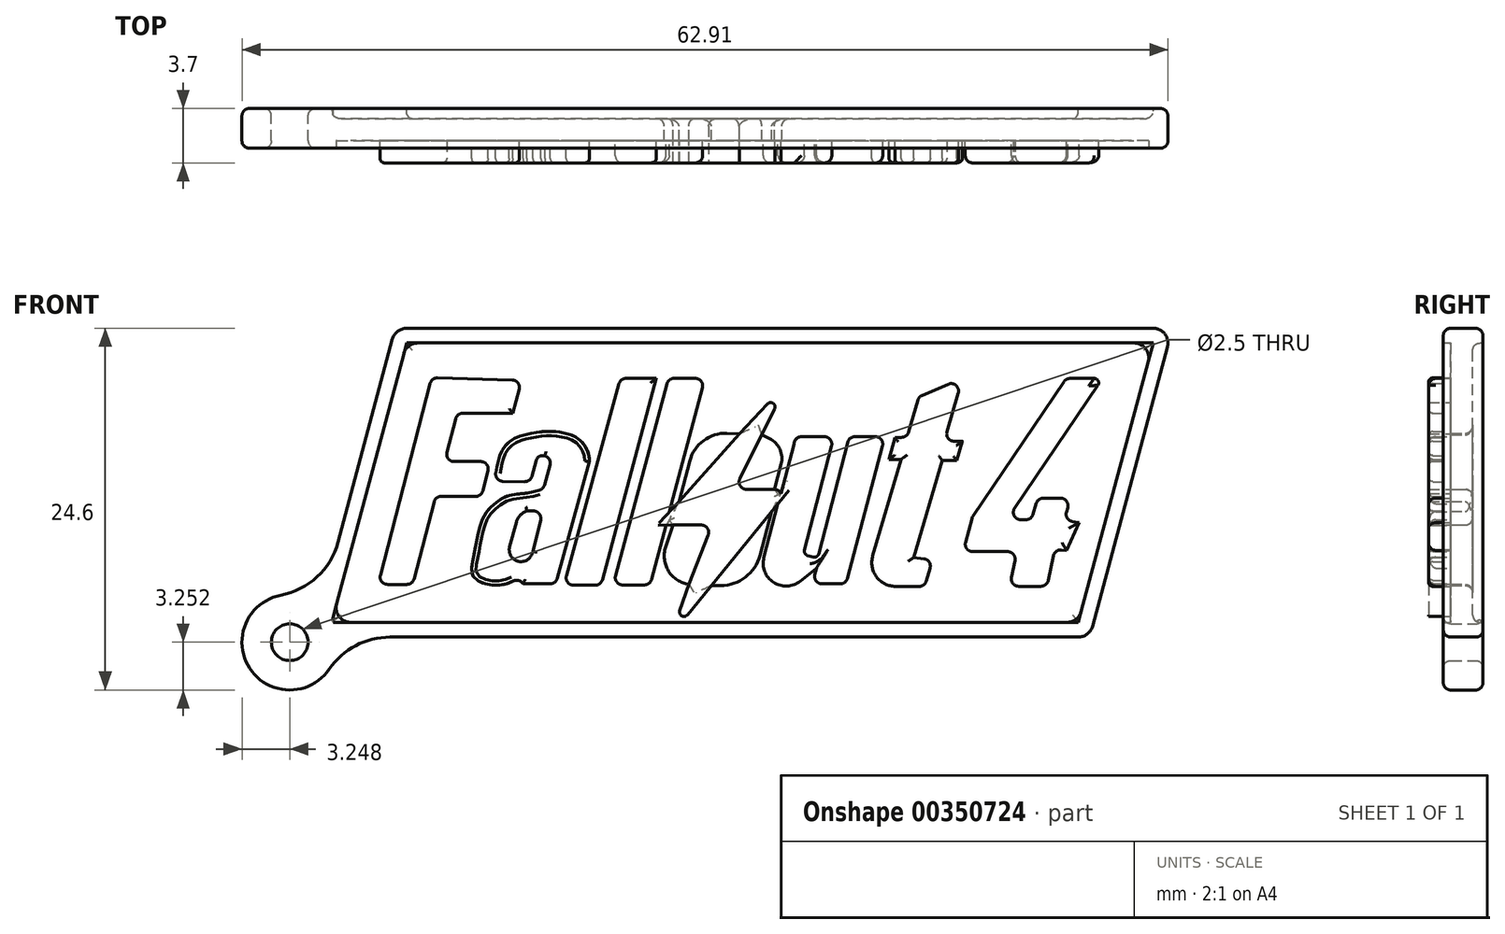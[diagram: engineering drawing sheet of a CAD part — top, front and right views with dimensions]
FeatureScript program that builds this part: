
annotation { "Feature Type Name" : "Feature", "Feature Type Description" : "" }
export const myFeature = defineFeature(function(context is Context, id is Id, definition is map)
    precondition{}
    {
        {
            var Q0;
            Q0=qCreatedBy(makeId("Front.planeOp"),FACE);
            var sketch = newSketch(context, id + "F0", { "sketchPlane" : qUnion([Q0])});
            skLineSegment(sketch, "E0", {"start": v(-23.37, 27.5) * mm, "end": v(29.43, 27.5) * mm});
            skLineSegment(sketch, "E1", {"start": v(29.43, 27.5) * mm, "end": v(23.8, 6.5) * mm});
            skLineSegment(sketch, "E2", {"start": v(23.8, 6.5) * mm, "end": v(-29, 6.5) * mm});
            skLineSegment(sketch, "E3", {"start": v(-29, 6.5) * mm, "end": v(-23.37, 27.5) * mm});
            skLineSegment(sketch, "E4", {"start": v(-20.9, 24.14) * mm, "end": v(-24.55, 10.08) * mm});
            skLineSegment(sketch, "E5", {"start": v(-24.55, 10.08) * mm, "end": v(-22.2, 10.08) * mm});
            skLineSegment(sketch, "E6", {"start": v(-22.2, 10.08) * mm, "end": v(-20.64, 16.07) * mm});
            skLineSegment(sketch, "E7", {"start": v(-20.64, 16.07) * mm, "end": v(-17.53, 16.07) * mm});
            skLineSegment(sketch, "E8", {"start": v(-17.53, 16.07) * mm, "end": v(-16.92, 18.43) * mm});
            skLineSegment(sketch, "E9", {"start": v(-16.92, 18.43) * mm, "end": v(-20.03, 18.43) * mm});
            skLineSegment(sketch, "E10", {"start": v(-20.03, 18.43) * mm, "end": v(-19.17, 21.72) * mm});
            skLineSegment(sketch, "E11", {"start": v(-19.17, 21.72) * mm, "end": v(-15.38, 21.72) * mm});
            skLineSegment(sketch, "E12", {"start": v(-15.38, 21.72) * mm, "end": v(-14.8, 23.97) * mm});
            skLineSegment(sketch, "E13", {"start": v(-14.8, 23.97) * mm, "end": v(-20.9, 24.14) * mm});
            skFitSpline(sketch, "E14", {"points": [v(-16.65, 17.1) * mm, v(-16.18, 19.06) * mm, v(-15.46, 19.9) * mm, v(-14.06, 20.38) * mm, v(-12.35, 20.46) * mm, v(-10.83, 19.9) * mm, v(-10.23, 18.9) * mm, v(-10.2, 18.43) * mm], "startDerivative": vector(2.12, 12.27) * mm, "endDerivative": vector(-0.12, -4.9) * mm});
            skLineSegment(sketch, "E15", {"start": v(-10.2, 18.43) * mm, "end": v(-12.47, 10.12) * mm});
            skLineSegment(sketch, "E16", {"start": v(-12.47, 10.12) * mm, "end": v(-14.7, 10.12) * mm});
            skLineSegment(sketch, "E17", {"start": v(-14.7, 10.12) * mm, "end": v(-14.7, 10.72) * mm});
            skFitSpline(sketch, "E18", {"points": [v(-14.7, 10.72) * mm, v(-15.82, 10.12) * mm, v(-17.3, 10.12) * mm, v(-18.13, 10.72) * mm, v(-18.1, 11.8) * mm, v(-17.37, 14.67) * mm, v(-16.53, 15.63) * mm, v(-15.74, 16.1) * mm, v(-14.38, 16.3) * mm, v(-13.33, 16.53) * mm], "startDerivative": vector(-9.58, -6.56) * mm, "endDerivative": vector(9.96, 0.8) * mm});
            skLineSegment(sketch, "E19", {"start": v(-13.33, 16.53) * mm, "end": v(-12.86, 18.22) * mm});
            skLineSegment(sketch, "E20", {"start": v(-13.2, 18.83) * mm, "end": v(-13.2, 18.83) * mm});
            skLineSegment(sketch, "E21", {"start": v(-13.82, 18.48) * mm, "end": v(-14.2, 17.06) * mm});
            skLineSegment(sketch, "E22", {"start": v(-14.2, 17.06) * mm, "end": v(-16.65, 17.1) * mm});
            skPoint(sketch, "E23.visualSharp", {"position": v(-15.68, 15.01) * mm});
            skLineSegment(sketch, "E24", {"start": v(-8.07, 24.1) * mm, "end": v(-11.92, 10.02) * mm});
            skLineSegment(sketch, "E25", {"start": v(-11.92, 10.02) * mm, "end": v(-9.4, 10.02) * mm});
            skLineSegment(sketch, "E26", {"start": v(-9.4, 10.02) * mm, "end": v(-5.64, 24.1) * mm});
            skLineSegment(sketch, "E27", {"start": v(-5.64, 24.1) * mm, "end": v(-8.07, 24.1) * mm});
            skPoint(sketch, "E28.visualSharp", {"position": v(-13.69, 18.96) * mm});
            skArc(sketch, "E28.filletArc", {"start": v(-13.2, 18.83) * mm, "mid": v(-13.59, 18.78) * mm, "end": v(-13.82, 18.48) * mm});
            skPoint(sketch, "E29.visualSharp", {"position": v(-12.73, 18.7) * mm});
            skArc(sketch, "E29.filletArc", {"start": v(-12.86, 18.22) * mm, "mid": v(-12.91, 18.6) * mm, "end": v(-13.21, 18.83) * mm});
            skArc(sketch, "E30.filletArc", {"start": v(-13.2, 18.83) * mm, "mid": v(-13.2, 18.83) * mm, "end": v(-13.2, 18.83) * mm});
            skLineSegment(sketch, "E31", {"start": v(-4.82, 24.1) * mm, "end": v(-8.58, 10.05) * mm});
            skLineSegment(sketch, "E32", {"start": v(-8.58, 10.05) * mm, "end": v(-6.06, 10.05) * mm});
            skLineSegment(sketch, "E33", {"start": v(-6.06, 10.05) * mm, "end": v(-2.34, 24.1) * mm});
            skLineSegment(sketch, "E34", {"start": v(-2.34, 24.1) * mm, "end": v(-4.82, 24.1) * mm});
            skLineSegment(sketch, "E35", {"start": v(-3.37, 18.47) * mm, "end": v(-4.1, 15.72) * mm});
            skLineSegment(sketch, "E36", {"start": v(-4.1, 15.72) * mm, "end": v(-4.75, 15.03) * mm});
            skLineSegment(sketch, "E37", {"start": v(-4.99, 14.11) * mm, "end": v(-4.5, 14.12) * mm});
            skLineSegment(sketch, "E38", {"start": v(-4.5, 14.12) * mm, "end": v(-5, 12.61) * mm});
            skLineSegment(sketch, "E39", {"start": v(-3.42, 10.08) * mm, "end": v(-4.04, 8.3) * mm});
            skLineSegment(sketch, "E40", {"start": v(-3.53, 8) * mm, "end": v(2.77, 15.73) * mm});
            skLineSegment(sketch, "E41", {"start": v(2.38, 16.55) * mm, "end": v(-0.32, 16.55) * mm});
            skLineSegment(sketch, "E42", {"start": v(-0.32, 16.55) * mm, "end": v(2.4, 22.01) * mm});
            skLineSegment(sketch, "E43", {"start": v(1.92, 22.35) * mm, "end": v(0, 20.34) * mm});
            skLineSegment(sketch, "E44", {"start": v(0, 20.34) * mm, "end": v(-0.84, 20.36) * mm});
            skArc(sketch, "E45", {"start": v(-0.84, 20.36) * mm, "mid": v(-2.43, 19.86) * mm, "end": v(-3.37, 18.47) * mm});
            skArc(sketch, "E46", {"start": v(-5, 12.61) * mm, "mid": v(-4.8, 10.98) * mm, "end": v(-3.42, 10.08) * mm});
            skLineSegment(sketch, "E47", {"start": v(-1.9, 10) * mm, "end": v(-1.26, 10) * mm});
            skLineSegment(sketch, "E48", {"start": v(2.2, 15.04) * mm, "end": v(1.4, 12.05) * mm});
            skArc(sketch, "E49", {"start": v(-1.26, 10) * mm, "mid": v(0.42, 10.58) * mm, "end": v(1.4, 12.05) * mm});
            skLineSegment(sketch, "E50", {"start": v(2.38, 16.55) * mm, "end": v(2.84, 18.25) * mm});
            skLineSegment(sketch, "E51", {"start": v(1.53, 20.26) * mm, "end": v(2.05, 20) * mm});
            skArc(sketch, "E52", {"start": v(2.84, 18.25) * mm, "mid": v(2.76, 19.26) * mm, "end": v(2.05, 20) * mm});
            skPoint(sketch, "E53.visualSharp", {"position": v(3.43, 16.55) * mm});
            skArc(sketch, "E53.filletArc", {"start": v(2.77, 15.73) * mm, "mid": v(2.83, 16.26) * mm, "end": v(2.38, 16.55) * mm});
            skPoint(sketch, "E54.visualSharp", {"position": v(-4.6, 6.7) * mm});
            skArc(sketch, "E54.filletArc", {"start": v(-4.04, 8.3) * mm, "mid": v(-3.9, 7.94) * mm, "end": v(-3.53, 8) * mm});
            skPoint(sketch, "E55.visualSharp", {"position": v(3.3, 23.8) * mm});
            skArc(sketch, "E55.filletArc", {"start": v(2.4, 22.01) * mm, "mid": v(2.3, 22.4) * mm, "end": v(1.92, 22.35) * mm});
            skLineSegment(sketch, "E56", {"start": v(3.84, 20.13) * mm, "end": v(2.83, 16.26) * mm});
            skLineSegment(sketch, "E57", {"start": v(2.63, 15.55) * mm, "end": v(1.67, 11.9) * mm});
            skLineSegment(sketch, "E58", {"start": v(3.84, 20.13) * mm, "end": v(6.43, 20.13) * mm});
            skLineSegment(sketch, "E59", {"start": v(6.43, 20.13) * mm, "end": v(4.43, 12.41) * mm});
            skLineSegment(sketch, "E60", {"start": v(4.64, 12.05) * mm, "end": v(5.03, 11.95) * mm});
            skLineSegment(sketch, "E61", {"start": v(5.4, 12.16) * mm, "end": v(7.46, 20.13) * mm});
            skLineSegment(sketch, "E62", {"start": v(7.46, 20.13) * mm, "end": v(9.9, 20.13) * mm});
            skLineSegment(sketch, "E63", {"start": v(9.9, 20.13) * mm, "end": v(7.25, 10.12) * mm});
            skLineSegment(sketch, "E64", {"start": v(7.25, 10.12) * mm, "end": v(5, 10.12) * mm});
            skLineSegment(sketch, "E65", {"start": v(5, 10.12) * mm, "end": v(5.23, 11.18) * mm});
            skLineSegment(sketch, "E66", {"start": v(5.23, 11.18) * mm, "end": v(4.13, 10.3) * mm});
            skArc(sketch, "E67", {"start": v(1.67, 11.9) * mm, "mid": v(2.33, 10.22) * mm, "end": v(4.13, 10.3) * mm});
            skPoint(sketch, "E68.visualSharp", {"position": v(4.35, 12.12) * mm});
            skArc(sketch, "E68.filletArc", {"start": v(4.43, 12.41) * mm, "mid": v(4.46, 12.18) * mm, "end": v(4.64, 12.05) * mm});
            skPoint(sketch, "E69.visualSharp", {"position": v(5.32, 11.87) * mm});
            skArc(sketch, "E69.filletArc", {"start": v(5.03, 11.95) * mm, "mid": v(5.26, 11.98) * mm, "end": v(5.4, 12.16) * mm});
            skLineSegment(sketch, "E70", {"start": v(15.17, 24.12) * mm, "end": v(12.2, 22.84) * mm});
            skLineSegment(sketch, "E71", {"start": v(12.2, 22.84) * mm, "end": v(11.4, 20.08) * mm});
            skLineSegment(sketch, "E72", {"start": v(11.4, 20.08) * mm, "end": v(10.57, 20.08) * mm});
            skLineSegment(sketch, "E73", {"start": v(10.57, 20.08) * mm, "end": v(10.17, 18.58) * mm});
            skLineSegment(sketch, "E74", {"start": v(10.17, 18.58) * mm, "end": v(11, 18.58) * mm});
            skLineSegment(sketch, "E75", {"start": v(11, 18.58) * mm, "end": v(9.06, 12.03) * mm});
            skLineSegment(sketch, "E76", {"start": v(10.63, 9.94) * mm, "end": v(12.6, 9.94) * mm});
            skLineSegment(sketch, "E77", {"start": v(12.6, 9.94) * mm, "end": v(13.12, 11.76) * mm});
            skLineSegment(sketch, "E78", {"start": v(13.12, 11.76) * mm, "end": v(11.86, 11.91) * mm});
            skLineSegment(sketch, "E79", {"start": v(11.86, 11.91) * mm, "end": v(13.8, 18.5) * mm});
            skLineSegment(sketch, "E80", {"start": v(13.8, 18.5) * mm, "end": v(14.77, 18.5) * mm});
            skLineSegment(sketch, "E81", {"start": v(14.77, 18.5) * mm, "end": v(15.15, 19.82) * mm});
            skLineSegment(sketch, "E82", {"start": v(15.15, 19.82) * mm, "end": v(13.92, 19.82) * mm});
            skLineSegment(sketch, "E83", {"start": v(13.92, 19.82) * mm, "end": v(15.17, 24.12) * mm});
            skArc(sketch, "E84", {"start": v(9.06, 12.03) * mm, "mid": v(9.32, 10.6) * mm, "end": v(10.63, 9.94) * mm});
            skCircle(sketch, "E85", {"center": v(15.6, 22.92) * mm, "radius": 0.4 * mm});
            skLineSegment(sketch, "E86", {"start": v(22.2, 24.09) * mm, "end": v(15.83, 14.66) * mm});
            skLineSegment(sketch, "E87", {"start": v(15.83, 14.66) * mm, "end": v(15.2, 12.3) * mm});
            skLineSegment(sketch, "E88", {"start": v(15.2, 12.3) * mm, "end": v(18.85, 12.3) * mm});
            skLineSegment(sketch, "E89", {"start": v(18.85, 12.3) * mm, "end": v(18.37, 9.95) * mm});
            skLineSegment(sketch, "E90", {"start": v(18.37, 9.95) * mm, "end": v(20.91, 9.95) * mm});
            skLineSegment(sketch, "E91", {"start": v(20.91, 9.95) * mm, "end": v(21.43, 12.46) * mm});
            skLineSegment(sketch, "E92", {"start": v(21.43, 12.46) * mm, "end": v(22.24, 12.4) * mm});
            skLineSegment(sketch, "E93", {"start": v(22.24, 12.4) * mm, "end": v(23.1, 14.29) * mm});
            skLineSegment(sketch, "E94", {"start": v(23.1, 14.29) * mm, "end": v(22.07, 14.45) * mm});
            skLineSegment(sketch, "E95", {"start": v(22.07, 14.45) * mm, "end": v(22.5, 15.95) * mm});
            skLineSegment(sketch, "E96", {"start": v(22.5, 15.95) * mm, "end": v(20.28, 15.95) * mm});
            skLineSegment(sketch, "E97", {"start": v(20.28, 15.95) * mm, "end": v(19.85, 14.48) * mm});
            skLineSegment(sketch, "E98", {"start": v(19.85, 14.48) * mm, "end": v(18.18, 14.48) * mm});
            skLineSegment(sketch, "E99", {"start": v(18.18, 14.48) * mm, "end": v(24.37, 23.62) * mm});
            skLineSegment(sketch, "E100", {"start": v(24.12, 24.09) * mm, "end": v(22.2, 24.09) * mm});
            skPoint(sketch, "E101.visualSharp", {"position": v(24.68, 24.09) * mm});
            skArc(sketch, "E101.filletArc", {"start": v(24.37, 23.62) * mm, "mid": v(24.38, 23.93) * mm, "end": v(24.12, 24.09) * mm});
            skLineSegment(sketch, "E102.0", {"start": v(-22.6, 26.5) * mm, "end": v(28.12, 26.5) * mm});
            skLineSegment(sketch, "E102.1", {"start": v(-27.7, 7.5) * mm, "end": v(-22.6, 26.5) * mm});
            skLineSegment(sketch, "E102.2", {"start": v(23.03, 7.5) * mm, "end": v(-27.7, 7.5) * mm});
            skLineSegment(sketch, "E102.3", {"start": v(28.12, 26.5) * mm, "end": v(23.03, 7.5) * mm});
            skLineSegment(sketch, "E103", {"start": v(-4.1, 15.72) * mm, "end": v(0, 20.34) * mm});
            skLineSegment(sketch, "E104", {"start": v(-4.5, 14.12) * mm, "end": v(-1.85, 14.12) * mm});
            skLineSegment(sketch, "E105", {"start": v(-1.85, 14.12) * mm, "end": v(-3.42, 10.08) * mm});
            skLineSegment(sketch, "E106", {"start": v(-13.34, 15.08) * mm, "end": v(-14.04, 12.33) * mm});
            skLineSegment(sketch, "E107", {"start": v(-13.34, 15.08) * mm, "end": v(-14.44, 15.08) * mm});
            skLineSegment(sketch, "E108", {"start": v(-15.14, 14.32) * mm, "end": v(-15.6, 12.64) * mm});
            skArc(sketch, "E109", {"start": v(-14.44, 15.08) * mm, "mid": v(-14.88, 14.78) * mm, "end": v(-15.14, 14.32) * mm});
            skArc(sketch, "E110", {"start": v(-15.6, 12.64) * mm, "mid": v(-14.99, 11.65) * mm, "end": v(-14.04, 12.33) * mm});
            skSolve(sketch);
        }
        {
            var Q0;
            Q0=makeQuery(id+"F0.imprint","IMPRINT",FACE,{"disambiguationData":[TD([[makeQuery(id+"F0.imprint","IMPRINT",EDGE,{"derivedFrom":sQuery(id+"F0.wireOp",EDGE,"E4")}),1.0]])]});
            var Q1;
            Q1=makeQuery(id+"F0.imprint","IMPRINT",FACE,{"disambiguationData":[TD([[makeQuery(id+"F0.imprint","IMPRINT",EDGE,{"derivedFrom":sQuery(id+"F0.wireOp",EDGE,"E14")}),-1.0]])]});
            var Q2;
            Q2=makeQuery(id+"F0.imprint","IMPRINT",FACE,{"disambiguationData":[TD([[makeQuery(id+"F0.imprint","IMPRINT",EDGE,{"derivedFrom":sQuery(id+"F0.wireOp",EDGE,"E24")}),1.0]])]});
            var Q3;
            Q3=makeQuery(id+"F0.imprint","IMPRINT",FACE,{"disambiguationData":[TD([[makeQuery(id+"F0.imprint","IMPRINT",EDGE,{"derivedFrom":sQuery(id+"F0.wireOp",EDGE,"E31")}),1.0]])]});
            var Q4;
            {var subQ12=sQuery(id+"F0.wireOp",EDGE,"E36");Q4=makeQuery(id+"F0.imprint","IMPRINT",FACE,{"disambiguationData":[TD([[makeQuery(id+"F0.imprint","IMPRINT",EDGE,{"derivedFrom":subQ12}),1.0]])]});}
            var Q5;
            {var subQ4=sQuery(id+"F0.wireOp",EDGE,"E56");Q5=makeQuery(id+"F0.imprint","IMPRINT",FACE,{"disambiguationData":[TD([[makeQuery(id+"F0.imprint","IMPRINT",EDGE,{"derivedFrom":subQ4}),1.0]])]});}
            var Q6;
            Q6=makeQuery(id+"F0.imprint","IMPRINT",FACE,{"disambiguationData":[TD([[makeQuery(id+"F0.imprint","IMPRINT",EDGE,{"derivedFrom":sQuery(id+"F0.wireOp",EDGE,"E70")}),1.0]])]});
            var Q7;
            Q7=makeQuery(id+"F0.imprint","IMPRINT",FACE,{"disambiguationData":[TD([[makeQuery(id+"F0.imprint","IMPRINT",EDGE,{"derivedFrom":sQuery(id+"F0.wireOp",EDGE,"E86")}),1.0]])]});
            extrude(context, id + "F1", {"entities" : qUnion([Q0, Q1, Q2, Q3, Q4, Q5, Q6, Q7]), "depth" : 3 * mm});
        }
        {
            var Q0;
            Q0=makeQuery(id+"F0.imprint","IMPRINT",FACE,{"disambiguationData":[TD([[makeQuery(id+"F0.imprint","IMPRINT",EDGE,{"derivedFrom":sQuery(id+"F0.wireOp",EDGE,"E35")}),1.0]])]});
            var Q1;
            Q1=makeQuery(id+"F0.imprint","IMPRINT",FACE,{"disambiguationData":[TD([[makeQuery(id+"F0.imprint","IMPRINT",EDGE,{"derivedFrom":sQuery(id+"F0.wireOp",EDGE,"E38")}),1.0]])]});
            var Q2;
            {var subQ2=sQuery(id+"F0.wireOp",EDGE,"E41");Q2=makeQuery(id+"F0.imprint","IMPRINT",FACE,{"disambiguationData":[TD([[makeQuery(id+"F0.imprint","IMPRINT",EDGE,{"derivedFrom":subQ2}),-1.0]])]});}
            var Q3;
            {var subQ0=sQuery(id+"F0.wireOp",EDGE,"E47");Q3=makeQuery(id+"F0.imprint","IMPRINT",FACE,{"disambiguationData":[TD([[makeQuery(id+"F0.imprint","IMPRINT",EDGE,{"derivedFrom":subQ0}),1.0]])]});}
            extrude(context, id + "F2", {"entities" : qUnion([Q0, Q1, Q2, Q3]), "operationType" : NewBodyOperationType.ADD, "depth" : 1 * mm});
        }
        {
            var Q0;
            Q0=makeQuery(id+"F0.imprint","IMPRINT",FACE,{"disambiguationData":[TD([[makeQuery(id+"F0.imprint","IMPRINT",EDGE,{"derivedFrom":sQuery(id+"F0.wireOp",EDGE,"E0")}),-1.0]])]});
            extrude(context, id + "F3", {"entities" : qUnion([Q0]), "depth" : 2 * mm, "hasSecondDirection" : true, "secondDirectionOppositeDirection" : true, "secondDirectionDepth" : .7 * mm});
        }
        {
            var Q0;
            Q0=makeQuery(id+"F0.imprint","IMPRINT",FACE,{"disambiguationData":[TD([[makeQuery(id+"F0.imprint","IMPRINT",EDGE,{"derivedFrom":sQuery(id+"F0.wireOp",EDGE,"E4")}),-1.0]])]});
            var Q1;
            Q1=makeQuery(id+"F0.imprint","IMPRINT",FACE,{"disambiguationData":[TD([[makeQuery(id+"F0.imprint","IMPRINT",EDGE,{"derivedFrom":sQuery(id+"F0.wireOp",EDGE,"E106")}),-1.0]])]});
            var Q2;
            Q2=makeQuery(id+"F0.imprint","IMPRINT",FACE,{"disambiguationData":[TD([[makeQuery(id+"F0.imprint","IMPRINT",EDGE,{"derivedFrom":sQuery(id+"F0.wireOp",EDGE,"E85")}),1.0]])]});
            extrude(context, id + "F4", {"entities" : qUnion([Q0, Q1, Q2]), "depth" : 1.5 * mm});
        }
        {
            var Q0;
            Q0=makeQuery(id+"F2.opExtrude","CAP_FACE",FACE,{"disambiguationData":[OSD([sQuery(id+"F0.wireOp",EDGE,"E41"),sQuery(id+"F0.wireOp",EDGE,"E42"),sQuery(id+"F0.wireOp",EDGE,"E50"),sQuery(id+"F0.wireOp",EDGE,"E51"),sQuery(id+"F0.wireOp",EDGE,"E52")])],"isStart":false});
            var Q1;
            Q1=makeQuery(id+"F2.opExtrude","CAP_FACE",FACE,{"disambiguationData":[OSD([sQuery(id+"F0.wireOp",EDGE,"E35"),sQuery(id+"F0.wireOp",EDGE,"E44"),sQuery(id+"F0.wireOp",EDGE,"E45"),sQuery(id+"F0.wireOp",EDGE,"E103")])],"isStart":false});
            var Q2;
            Q2=makeQuery(id+"F2.opExtrude","CAP_FACE",FACE,{"disambiguationData":[OSD([sQuery(id+"F0.wireOp",EDGE,"E38"),sQuery(id+"F0.wireOp",EDGE,"E46"),sQuery(id+"F0.wireOp",EDGE,"E104"),sQuery(id+"F0.wireOp",EDGE,"E105")])],"isStart":false});
            var Q3;
            Q3=makeQuery(id+"F2.opExtrude","CAP_FACE",FACE,{"disambiguationData":[OSD([sQuery(id+"F0.wireOp",EDGE,"E40"),sQuery(id+"F0.wireOp",EDGE,"E47"),sQuery(id+"F0.wireOp",EDGE,"E48"),sQuery(id+"F0.wireOp",EDGE,"E49")])],"isStart":false});
            extrude(context, id + "F5", {"entities" : qUnion([Q0, Q1, Q2, Q3]), "operationType" : NewBodyOperationType.REMOVE, "oppositeDirection" : true, "depth" : 25 * mm});
        }
        {
            var Q0;
            Q0=makeQuery(id+"F3.opExtrude","SWEPT_BODY",BODY,{"disambiguationData":[OSD([sQuery(id+"F0.wireOp",EDGE,"E0"),sQuery(id+"F0.wireOp",EDGE,"E1"),sQuery(id+"F0.wireOp",EDGE,"E2"),sQuery(id+"F0.wireOp",EDGE,"E3"),sQuery(id+"F0.wireOp",EDGE,"E102.0"),sQuery(id+"F0.wireOp",EDGE,"E102.1"),sQuery(id+"F0.wireOp",EDGE,"E102.2"),sQuery(id+"F0.wireOp",EDGE,"E102.3")])]});
            var Q1;
            Q1=makeQuery(id+"F4.opExtrude","SWEPT_BODY",BODY,{"disambiguationData":[OSD([sQuery(id+"F0.wireOp",EDGE,"E4"),sQuery(id+"F0.wireOp",EDGE,"E5"),sQuery(id+"F0.wireOp",EDGE,"E6"),sQuery(id+"F0.wireOp",EDGE,"E7"),sQuery(id+"F0.wireOp",EDGE,"E8"),sQuery(id+"F0.wireOp",EDGE,"E9"),sQuery(id+"F0.wireOp",EDGE,"E10"),sQuery(id+"F0.wireOp",EDGE,"E11"),sQuery(id+"F0.wireOp",EDGE,"E12"),sQuery(id+"F0.wireOp",EDGE,"E13"),sQuery(id+"F0.wireOp",EDGE,"E14"),sQuery(id+"F0.wireOp",EDGE,"E15"),sQuery(id+"F0.wireOp",EDGE,"E16"),sQuery(id+"F0.wireOp",EDGE,"E17"),sQuery(id+"F0.wireOp",EDGE,"E18"),sQuery(id+"F0.wireOp",EDGE,"E19"),sQuery(id+"F0.wireOp",EDGE,"E21"),sQuery(id+"F0.wireOp",EDGE,"E22"),sQuery(id+"F0.wireOp",EDGE,"E24"),sQuery(id+"F0.wireOp",EDGE,"E25"),sQuery(id+"F0.wireOp",EDGE,"E26"),sQuery(id+"F0.wireOp",EDGE,"E27"),sQuery(id+"F0.wireOp",EDGE,"E28.filletArc"),sQuery(id+"F0.wireOp",EDGE,"E29.filletArc"),sQuery(id+"F0.wireOp",EDGE,"E31"),sQuery(id+"F0.wireOp",EDGE,"E32"),sQuery(id+"F0.wireOp",EDGE,"E33"),sQuery(id+"F0.wireOp",EDGE,"E34"),sQuery(id+"F0.wireOp",EDGE,"E35"),sQuery(id+"F0.wireOp",EDGE,"E36"),sQuery(id+"F0.wireOp",EDGE,"E37"),sQuery(id+"F0.wireOp",EDGE,"E38"),sQuery(id+"F0.wireOp",EDGE,"E39"),sQuery(id+"F0.wireOp",EDGE,"E40"),sQuery(id+"F0.wireOp",EDGE,"E42"),sQuery(id+"F0.wireOp",EDGE,"E43"),sQuery(id+"F0.wireOp",EDGE,"E44"),sQuery(id+"F0.wireOp",EDGE,"E45"),sQuery(id+"F0.wireOp",EDGE,"E46"),sQuery(id+"F0.wireOp",EDGE,"E47"),sQuery(id+"F0.wireOp",EDGE,"E48"),sQuery(id+"F0.wireOp",EDGE,"E49"),sQuery(id+"F0.wireOp",EDGE,"E50"),sQuery(id+"F0.wireOp",EDGE,"E51"),sQuery(id+"F0.wireOp",EDGE,"E52"),sQuery(id+"F0.wireOp",EDGE,"E53.filletArc"),sQuery(id+"F0.wireOp",EDGE,"E54.filletArc"),sQuery(id+"F0.wireOp",EDGE,"E55.filletArc"),sQuery(id+"F0.wireOp",EDGE,"E56"),sQuery(id+"F0.wireOp",EDGE,"E57"),sQuery(id+"F0.wireOp",EDGE,"E58"),sQuery(id+"F0.wireOp",EDGE,"E59"),sQuery(id+"F0.wireOp",EDGE,"E60"),sQuery(id+"F0.wireOp",EDGE,"E61"),sQuery(id+"F0.wireOp",EDGE,"E62"),sQuery(id+"F0.wireOp",EDGE,"E63"),sQuery(id+"F0.wireOp",EDGE,"E64"),sQuery(id+"F0.wireOp",EDGE,"E65"),sQuery(id+"F0.wireOp",EDGE,"E66"),sQuery(id+"F0.wireOp",EDGE,"E67"),sQuery(id+"F0.wireOp",EDGE,"E68.filletArc"),sQuery(id+"F0.wireOp",EDGE,"E69.filletArc"),sQuery(id+"F0.wireOp",EDGE,"E70"),sQuery(id+"F0.wireOp",EDGE,"E71"),sQuery(id+"F0.wireOp",EDGE,"E72"),sQuery(id+"F0.wireOp",EDGE,"E73"),sQuery(id+"F0.wireOp",EDGE,"E74"),sQuery(id+"F0.wireOp",EDGE,"E75"),sQuery(id+"F0.wireOp",EDGE,"E76"),sQuery(id+"F0.wireOp",EDGE,"E77"),sQuery(id+"F0.wireOp",EDGE,"E78"),sQuery(id+"F0.wireOp",EDGE,"E79"),sQuery(id+"F0.wireOp",EDGE,"E80"),sQuery(id+"F0.wireOp",EDGE,"E81"),sQuery(id+"F0.wireOp",EDGE,"E82"),sQuery(id+"F0.wireOp",EDGE,"E83"),sQuery(id+"F0.wireOp",EDGE,"E84"),sQuery(id+"F0.wireOp",EDGE,"E85"),sQuery(id+"F0.wireOp",EDGE,"E86"),sQuery(id+"F0.wireOp",EDGE,"E87"),sQuery(id+"F0.wireOp",EDGE,"E88"),sQuery(id+"F0.wireOp",EDGE,"E89"),sQuery(id+"F0.wireOp",EDGE,"E90"),sQuery(id+"F0.wireOp",EDGE,"E91"),sQuery(id+"F0.wireOp",EDGE,"E92"),sQuery(id+"F0.wireOp",EDGE,"E93"),sQuery(id+"F0.wireOp",EDGE,"E94"),sQuery(id+"F0.wireOp",EDGE,"E95"),sQuery(id+"F0.wireOp",EDGE,"E96"),sQuery(id+"F0.wireOp",EDGE,"E97"),sQuery(id+"F0.wireOp",EDGE,"E98"),sQuery(id+"F0.wireOp",EDGE,"E99"),sQuery(id+"F0.wireOp",EDGE,"E100"),sQuery(id+"F0.wireOp",EDGE,"E101.filletArc"),sQuery(id+"F0.wireOp",EDGE,"E102.0"),sQuery(id+"F0.wireOp",EDGE,"E102.1"),sQuery(id+"F0.wireOp",EDGE,"E102.2"),sQuery(id+"F0.wireOp",EDGE,"E102.3")])]});
            var Q2;
            Q2=makeQuery(id+"F1.opExtrude","SWEPT_BODY",BODY,{"disambiguationData":[OSD([sQuery(id+"F0.wireOp",EDGE,"E4"),sQuery(id+"F0.wireOp",EDGE,"E5"),sQuery(id+"F0.wireOp",EDGE,"E6"),sQuery(id+"F0.wireOp",EDGE,"E7"),sQuery(id+"F0.wireOp",EDGE,"E8"),sQuery(id+"F0.wireOp",EDGE,"E9"),sQuery(id+"F0.wireOp",EDGE,"E10"),sQuery(id+"F0.wireOp",EDGE,"E11"),sQuery(id+"F0.wireOp",EDGE,"E12"),sQuery(id+"F0.wireOp",EDGE,"E13")])]});
            var Q3;
            Q3=makeQuery(id+"F1.opExtrude","SWEPT_BODY",BODY,{"disambiguationData":[OSD([sQuery(id+"F0.wireOp",EDGE,"E14"),sQuery(id+"F0.wireOp",EDGE,"E15"),sQuery(id+"F0.wireOp",EDGE,"E16"),sQuery(id+"F0.wireOp",EDGE,"E17"),sQuery(id+"F0.wireOp",EDGE,"E18"),sQuery(id+"F0.wireOp",EDGE,"E19"),sQuery(id+"F0.wireOp",EDGE,"E21"),sQuery(id+"F0.wireOp",EDGE,"E22"),sQuery(id+"F0.wireOp",EDGE,"u2CHap73-eIfQ-AhEI-1PnA-1sPRTdayhLp1"),sQuery(id+"F0.wireOp",EDGE,"4653361d-3eab-4c66-b073-450a15e5966c"),sQuery(id+"F0.wireOp",EDGE,"Ms8ezGKg-GFvZ-WPBB-vuYG-Pn63Gs3kcZVX"),sQuery(id+"F0.wireOp",EDGE,"8MuqAIwF-KjcQ-kyYc-nLWA-kJafWhadJyZa"),sQuery(id+"F0.wireOp",EDGE,"E23.filletArc"),sQuery(id+"F0.wireOp",EDGE,"E28.filletArc"),sQuery(id+"F0.wireOp",EDGE,"E29.filletArc")])]});
            var Q4;
            Q4=makeQuery(id+"F1.opExtrude","SWEPT_BODY",BODY,{"disambiguationData":[OSD([sQuery(id+"F0.wireOp",EDGE,"E24"),sQuery(id+"F0.wireOp",EDGE,"E25"),sQuery(id+"F0.wireOp",EDGE,"E26"),sQuery(id+"F0.wireOp",EDGE,"E27")])]});
            var Q5;
            Q5=makeQuery(id+"F1.opExtrude","SWEPT_BODY",BODY,{"disambiguationData":[OSD([sQuery(id+"F0.wireOp",EDGE,"E31"),sQuery(id+"F0.wireOp",EDGE,"E32"),sQuery(id+"F0.wireOp",EDGE,"E33"),sQuery(id+"F0.wireOp",EDGE,"E34"),sQuery(id+"F0.wireOp",EDGE,"E36"),sQuery(id+"F0.wireOp",EDGE,"E37"),sQuery(id+"F0.wireOp",EDGE,"E39"),sQuery(id+"F0.wireOp",EDGE,"E40"),sQuery(id+"F0.wireOp",EDGE,"E41"),sQuery(id+"F0.wireOp",EDGE,"E42"),sQuery(id+"F0.wireOp",EDGE,"E43"),sQuery(id+"F0.wireOp",EDGE,"E53.filletArc"),sQuery(id+"F0.wireOp",EDGE,"E54.filletArc"),sQuery(id+"F0.wireOp",EDGE,"E55.filletArc"),sQuery(id+"F0.wireOp",EDGE,"E56"),sQuery(id+"F0.wireOp",EDGE,"E57"),sQuery(id+"F0.wireOp",EDGE,"E58"),sQuery(id+"F0.wireOp",EDGE,"E59"),sQuery(id+"F0.wireOp",EDGE,"E60"),sQuery(id+"F0.wireOp",EDGE,"E61"),sQuery(id+"F0.wireOp",EDGE,"E62"),sQuery(id+"F0.wireOp",EDGE,"E63"),sQuery(id+"F0.wireOp",EDGE,"E64"),sQuery(id+"F0.wireOp",EDGE,"E65"),sQuery(id+"F0.wireOp",EDGE,"E66"),sQuery(id+"F0.wireOp",EDGE,"E67"),sQuery(id+"F0.wireOp",EDGE,"E68.filletArc"),sQuery(id+"F0.wireOp",EDGE,"E69.filletArc"),sQuery(id+"F0.wireOp",EDGE,"E103"),sQuery(id+"F0.wireOp",EDGE,"E104"),sQuery(id+"F0.wireOp",EDGE,"E105")])]});
            var Q6;
            Q6=makeQuery(id+"F1.opExtrude","SWEPT_BODY",BODY,{"disambiguationData":[OSD([sQuery(id+"F0.wireOp",EDGE,"E70"),sQuery(id+"F0.wireOp",EDGE,"E71"),sQuery(id+"F0.wireOp",EDGE,"E72"),sQuery(id+"F0.wireOp",EDGE,"E73"),sQuery(id+"F0.wireOp",EDGE,"E74"),sQuery(id+"F0.wireOp",EDGE,"E75"),sQuery(id+"F0.wireOp",EDGE,"E76"),sQuery(id+"F0.wireOp",EDGE,"E77"),sQuery(id+"F0.wireOp",EDGE,"E78"),sQuery(id+"F0.wireOp",EDGE,"E79"),sQuery(id+"F0.wireOp",EDGE,"E80"),sQuery(id+"F0.wireOp",EDGE,"E81"),sQuery(id+"F0.wireOp",EDGE,"E82"),sQuery(id+"F0.wireOp",EDGE,"E83"),sQuery(id+"F0.wireOp",EDGE,"E84")])]});
            var Q7;
            Q7=makeQuery(id+"F1.opExtrude","SWEPT_BODY",BODY,{"disambiguationData":[OSD([sQuery(id+"F0.wireOp",EDGE,"E86"),sQuery(id+"F0.wireOp",EDGE,"E87"),sQuery(id+"F0.wireOp",EDGE,"E88"),sQuery(id+"F0.wireOp",EDGE,"E89"),sQuery(id+"F0.wireOp",EDGE,"E90"),sQuery(id+"F0.wireOp",EDGE,"E91"),sQuery(id+"F0.wireOp",EDGE,"E92"),sQuery(id+"F0.wireOp",EDGE,"E93"),sQuery(id+"F0.wireOp",EDGE,"E94"),sQuery(id+"F0.wireOp",EDGE,"E95"),sQuery(id+"F0.wireOp",EDGE,"E96"),sQuery(id+"F0.wireOp",EDGE,"E97"),sQuery(id+"F0.wireOp",EDGE,"E98"),sQuery(id+"F0.wireOp",EDGE,"E99"),sQuery(id+"F0.wireOp",EDGE,"E100"),sQuery(id+"F0.wireOp",EDGE,"E101.filletArc")])]});
            var Q8;
            Q8=makeQuery(id+"F4.opExtrude","SWEPT_BODY",BODY,{"disambiguationData":[OSD([sQuery(id+"F0.wireOp",EDGE,"E106"),sQuery(id+"F0.wireOp",EDGE,"E107"),sQuery(id+"F0.wireOp",EDGE,"E108"),sQuery(id+"F0.wireOp",EDGE,"E109"),sQuery(id+"F0.wireOp",EDGE,"E110")])]});
            booleanBodies(context, id + "F6", {"operationType" : BooleanOperationType.UNION, "tools" : qUnion([Q0, Q1, Q2, Q3, Q4, Q5, Q6, Q7, Q8])});
        }
        {
            var Q0;
            {var subQ0=sQuery(id+"F0.wireOp",EDGE,"E102.3");var subQ1=sQuery(id+"F0.wireOp",EDGE,"E102.2");var subQ2=sQuery(id+"F0.wireOp",EDGE,"E102.1");var subQ3=sQuery(id+"F0.wireOp",EDGE,"E102.0");Q0=makeQuery(id+"F6.opBoolean","SPLIT",EDGE,{"disambiguationData":[TD([makeQuery(id+"F3.opExtrude","CAP_FACE",FACE,{"disambiguationData":[OSD([sQuery(id+"F0.wireOp",EDGE,"E0"),sQuery(id+"F0.wireOp",EDGE,"E1"),sQuery(id+"F0.wireOp",EDGE,"E2"),sQuery(id+"F0.wireOp",EDGE,"E3"),subQ3,subQ2,subQ1,subQ0])],"isStart":false})])],"derivedFrom":makeQuery(id+"F3.opExtrude","SWEPT_EDGE",EDGE,{"disambiguationData":[OSD([subQ3,subQ2])]})});}
            var Q1;
            {var subQ0=sQuery(id+"F0.wireOp",EDGE,"E102.3");var subQ1=sQuery(id+"F0.wireOp",EDGE,"E102.2");var subQ2=sQuery(id+"F0.wireOp",EDGE,"E102.1");var subQ3=sQuery(id+"F0.wireOp",EDGE,"E102.0");Q1=makeQuery(id+"F6.opBoolean","SPLIT",EDGE,{"disambiguationData":[TD([makeQuery(id+"F3.opExtrude","CAP_FACE",FACE,{"disambiguationData":[OSD([sQuery(id+"F0.wireOp",EDGE,"E0"),sQuery(id+"F0.wireOp",EDGE,"E1"),sQuery(id+"F0.wireOp",EDGE,"E2"),sQuery(id+"F0.wireOp",EDGE,"E3"),subQ3,subQ2,subQ1,subQ0])],"isStart":false})])],"derivedFrom":makeQuery(id+"F3.opExtrude","SWEPT_EDGE",EDGE,{"disambiguationData":[OSD([subQ3,subQ0])]})});}
            var Q2;
            {var subQ0=sQuery(id+"F0.wireOp",EDGE,"E102.3");var subQ1=sQuery(id+"F0.wireOp",EDGE,"E102.2");var subQ2=sQuery(id+"F0.wireOp",EDGE,"E102.1");var subQ3=sQuery(id+"F0.wireOp",EDGE,"E102.0");Q2=makeQuery(id+"F6.opBoolean","SPLIT",EDGE,{"disambiguationData":[TD([makeQuery(id+"F3.opExtrude","CAP_FACE",FACE,{"disambiguationData":[OSD([sQuery(id+"F0.wireOp",EDGE,"E0"),sQuery(id+"F0.wireOp",EDGE,"E1"),sQuery(id+"F0.wireOp",EDGE,"E2"),sQuery(id+"F0.wireOp",EDGE,"E3"),subQ3,subQ2,subQ1,subQ0])],"isStart":false})])],"derivedFrom":makeQuery(id+"F3.opExtrude","SWEPT_EDGE",EDGE,{"disambiguationData":[OSD([subQ1,subQ0])]})});}
            var Q3;
            {var subQ0=sQuery(id+"F0.wireOp",EDGE,"E102.3");var subQ1=sQuery(id+"F0.wireOp",EDGE,"E102.2");var subQ2=sQuery(id+"F0.wireOp",EDGE,"E102.1");var subQ3=sQuery(id+"F0.wireOp",EDGE,"E102.0");Q3=makeQuery(id+"F6.opBoolean","SPLIT",EDGE,{"disambiguationData":[TD([makeQuery(id+"F3.opExtrude","CAP_FACE",FACE,{"disambiguationData":[OSD([sQuery(id+"F0.wireOp",EDGE,"E0"),sQuery(id+"F0.wireOp",EDGE,"E1"),sQuery(id+"F0.wireOp",EDGE,"E2"),sQuery(id+"F0.wireOp",EDGE,"E3"),subQ3,subQ2,subQ1,subQ0])],"isStart":false})])],"derivedFrom":makeQuery(id+"F3.opExtrude","SWEPT_EDGE",EDGE,{"disambiguationData":[OSD([subQ2,subQ1])]})});}
            fillet(context, id + "F7", {"entities" : qUnion([Q0, Q1, Q2, Q3]), "radius" : 1 * mm, "tangentPropagation" : true, "allowEdgeOverflow" : false});
        }
        {
            var Q0;
            Q0=makeQuery(id+"F3.opExtrude","SWEPT_EDGE",EDGE,{"disambiguationData":[OSD([sQuery(id+"F0.wireOp",EDGE,"E2"),sQuery(id+"F0.wireOp",EDGE,"E3")])]});
            var Q1;
            Q1=makeQuery(id+"F3.opExtrude","SWEPT_EDGE",EDGE,{"disambiguationData":[OSD([sQuery(id+"F0.wireOp",EDGE,"E0"),sQuery(id+"F0.wireOp",EDGE,"E3")])]});
            var Q2;
            Q2=makeQuery(id+"F3.opExtrude","SWEPT_EDGE",EDGE,{"disambiguationData":[OSD([sQuery(id+"F0.wireOp",EDGE,"E1"),sQuery(id+"F0.wireOp",EDGE,"E2")])]});
            var Q3;
            Q3=makeQuery(id+"F3.opExtrude","SWEPT_EDGE",EDGE,{"disambiguationData":[OSD([sQuery(id+"F0.wireOp",EDGE,"E0"),sQuery(id+"F0.wireOp",EDGE,"E1")])]});
            fillet(context, id + "F8", {"entities" : qUnion([Q0, Q1, Q2, Q3]), "radius" : 1 * mm, "tangentPropagation" : true, "allowEdgeOverflow" : false});
        }
        {
            var Q0;
            Q0=makeQuery(id+"F1.opExtrude","SWEPT_EDGE",EDGE,{"disambiguationData":[OSD([sQuery(id+"F0.wireOp",EDGE,"E12"),sQuery(id+"F0.wireOp",EDGE,"E13")])]});
            var Q1;
            Q1=makeQuery(id+"F1.opExtrude","SWEPT_EDGE",EDGE,{"disambiguationData":[OSD([sQuery(id+"F0.wireOp",EDGE,"E4"),sQuery(id+"F0.wireOp",EDGE,"E13")])]});
            var Q2;
            Q2=makeQuery(id+"F1.opExtrude","SWEPT_EDGE",EDGE,{"disambiguationData":[OSD([sQuery(id+"F0.wireOp",EDGE,"E4"),sQuery(id+"F0.wireOp",EDGE,"E5")])]});
            var Q3;
            Q3=makeQuery(id+"F1.opExtrude","SWEPT_EDGE",EDGE,{"disambiguationData":[OSD([sQuery(id+"F0.wireOp",EDGE,"E5"),sQuery(id+"F0.wireOp",EDGE,"E6")])]});
            var Q4;
            Q4=makeQuery(id+"F1.opExtrude","SWEPT_EDGE",EDGE,{"disambiguationData":[OSD([sQuery(id+"F0.wireOp",EDGE,"E7"),sQuery(id+"F0.wireOp",EDGE,"E8")])]});
            var Q5;
            Q5=makeQuery(id+"F1.opExtrude","SWEPT_EDGE",EDGE,{"disambiguationData":[OSD([sQuery(id+"F0.wireOp",EDGE,"E8"),sQuery(id+"F0.wireOp",EDGE,"E9")])]});
            var Q6;
            Q6=makeQuery(id+"F1.opExtrude","SWEPT_EDGE",EDGE,{"disambiguationData":[OSD([sQuery(id+"F0.wireOp",EDGE,"E10"),sQuery(id+"F0.wireOp",EDGE,"E11")])]});
            var Q7;
            Q7=makeQuery(id+"F1.opExtrude","SWEPT_EDGE",EDGE,{"disambiguationData":[OSD([sQuery(id+"F0.wireOp",EDGE,"E9"),sQuery(id+"F0.wireOp",EDGE,"E10")])]});
            var Q8;
            Q8=makeQuery(id+"F1.opExtrude","SWEPT_EDGE",EDGE,{"disambiguationData":[OSD([sQuery(id+"F0.wireOp",EDGE,"E6"),sQuery(id+"F0.wireOp",EDGE,"E7")])]});
            var Q9;
            Q9=makeQuery(id+"F1.opExtrude","SWEPT_EDGE",EDGE,{"disambiguationData":[OSD([sQuery(id+"F0.wireOp",EDGE,"E17"),sQuery(id+"F0.wireOp",EDGE,"E18")])]});
            var Q10;
            Q10=makeQuery(id+"F1.opExtrude","SWEPT_EDGE",EDGE,{"disambiguationData":[OSD([sQuery(id+"F0.wireOp",EDGE,"E15"),sQuery(id+"F0.wireOp",EDGE,"E16")])]});
            var Q11;
            Q11=makeQuery(id+"F1.opExtrude","SWEPT_EDGE",EDGE,{"disambiguationData":[OSD([sQuery(id+"F0.wireOp",EDGE,"E106"),sQuery(id+"F0.wireOp",EDGE,"E107")])]});
            var Q12;
            Q12=makeQuery(id+"F1.opExtrude","SWEPT_EDGE",EDGE,{"disambiguationData":[OSD([sQuery(id+"F0.wireOp",EDGE,"E18"),sQuery(id+"F0.wireOp",EDGE,"E19")])]});
            var Q13;
            Q13=makeQuery(id+"F1.opExtrude","SWEPT_EDGE",EDGE,{"disambiguationData":[OSD([sQuery(id+"F0.wireOp",EDGE,"E21"),sQuery(id+"F0.wireOp",EDGE,"E22")])]});
            var Q14;
            Q14=makeQuery(id+"F1.opExtrude","SWEPT_EDGE",EDGE,{"disambiguationData":[OSD([sQuery(id+"F0.wireOp",EDGE,"E14"),sQuery(id+"F0.wireOp",EDGE,"E22")])]});
            var Q15;
            Q15=makeQuery(id+"F1.opExtrude","SWEPT_EDGE",EDGE,{"disambiguationData":[OSD([sQuery(id+"F0.wireOp",EDGE,"E24"),sQuery(id+"F0.wireOp",EDGE,"E25")])]});
            var Q16;
            Q16=makeQuery(id+"F1.opExtrude","SWEPT_EDGE",EDGE,{"disambiguationData":[OSD([sQuery(id+"F0.wireOp",EDGE,"E25"),sQuery(id+"F0.wireOp",EDGE,"E26")])]});
            var Q17;
            Q17=makeQuery(id+"F1.opExtrude","SWEPT_EDGE",EDGE,{"disambiguationData":[OSD([sQuery(id+"F0.wireOp",EDGE,"E24"),sQuery(id+"F0.wireOp",EDGE,"E27")])]});
            var Q18;
            Q18=makeQuery(id+"F1.opExtrude","SWEPT_EDGE",EDGE,{"disambiguationData":[OSD([sQuery(id+"F0.wireOp",EDGE,"E31"),sQuery(id+"F0.wireOp",EDGE,"E34")])]});
            var Q19;
            Q19=makeQuery(id+"F1.opExtrude","SWEPT_EDGE",EDGE,{"disambiguationData":[OSD([sQuery(id+"F0.wireOp",EDGE,"E33"),sQuery(id+"F0.wireOp",EDGE,"E34")])]});
            var Q20;
            Q20=makeQuery(id+"F1.opExtrude","SWEPT_EDGE",EDGE,{"disambiguationData":[OSD([sQuery(id+"F0.wireOp",EDGE,"E32"),sQuery(id+"F0.wireOp",EDGE,"E33")])]});
            var Q21;
            Q21=makeQuery(id+"F1.opExtrude","SWEPT_EDGE",EDGE,{"disambiguationData":[OSD([sQuery(id+"F0.wireOp",EDGE,"E31"),sQuery(id+"F0.wireOp",EDGE,"E32")])]});
            var Q22;
            {var subQ0=sQuery(id+"F0.wireOp",EDGE,"E42");var subQ1=sQuery(id+"F0.wireOp",EDGE,"E41");Q22=makeQuery(id+"F5.boolean.opBoolean","MERGE",EDGE,{"derivedFrom":[makeQuery(id+"F1.opExtrude","SWEPT_EDGE",EDGE,{"disambiguationData":[OSD([subQ1,subQ0])]}),makeQuery(id+"F5.opExtrude","SWEPT_EDGE",EDGE,{"disambiguationData":[OSD([subQ1,subQ0])]})]});}
            var Q23;
            {var subQ0=sQuery(id+"F0.wireOp",EDGE,"E105");var subQ1=sQuery(id+"F0.wireOp",EDGE,"E104");Q23=makeQuery(id+"F5.boolean.opBoolean","MERGE",EDGE,{"derivedFrom":[makeQuery(id+"F1.opExtrude","SWEPT_EDGE",EDGE,{"disambiguationData":[OSD([subQ1,subQ0])]}),makeQuery(id+"F5.opExtrude","SWEPT_EDGE",EDGE,{"disambiguationData":[OSD([subQ1,subQ0])]})]});}
            var Q24;
            Q24=makeQuery(id+"F1.opExtrude","SWEPT_EDGE",EDGE,{"disambiguationData":[OSD([sQuery(id+"F0.wireOp",EDGE,"E56"),sQuery(id+"F0.wireOp",EDGE,"E58")])]});
            var Q25;
            Q25=makeQuery(id+"F1.opExtrude","SWEPT_EDGE",EDGE,{"disambiguationData":[OSD([sQuery(id+"F0.wireOp",EDGE,"E58"),sQuery(id+"F0.wireOp",EDGE,"E59")])]});
            var Q26;
            Q26=makeQuery(id+"F1.opExtrude","SWEPT_EDGE",EDGE,{"disambiguationData":[OSD([sQuery(id+"F0.wireOp",EDGE,"E61"),sQuery(id+"F0.wireOp",EDGE,"E62")])]});
            var Q27;
            Q27=makeQuery(id+"F1.opExtrude","SWEPT_EDGE",EDGE,{"disambiguationData":[OSD([sQuery(id+"F0.wireOp",EDGE,"E62"),sQuery(id+"F0.wireOp",EDGE,"E63")])]});
            var Q28;
            Q28=makeQuery(id+"F1.opExtrude","SWEPT_EDGE",EDGE,{"disambiguationData":[OSD([sQuery(id+"F0.wireOp",EDGE,"E63"),sQuery(id+"F0.wireOp",EDGE,"E64")])]});
            var Q29;
            Q29=makeQuery(id+"F1.opExtrude","SWEPT_EDGE",EDGE,{"disambiguationData":[OSD([sQuery(id+"F0.wireOp",EDGE,"E64"),sQuery(id+"F0.wireOp",EDGE,"E65")])]});
            var Q30;
            Q30=makeQuery(id+"F1.opExtrude","SWEPT_EDGE",EDGE,{"disambiguationData":[OSD([sQuery(id+"F0.wireOp",EDGE,"E70"),sQuery(id+"F0.wireOp",EDGE,"E71")])]});
            var Q31;
            Q31=makeQuery(id+"F1.opExtrude","SWEPT_EDGE",EDGE,{"disambiguationData":[OSD([sQuery(id+"F0.wireOp",EDGE,"E70"),sQuery(id+"F0.wireOp",EDGE,"E83")])]});
            var Q32;
            Q32=makeQuery(id+"F1.opExtrude","SWEPT_EDGE",EDGE,{"disambiguationData":[OSD([sQuery(id+"F0.wireOp",EDGE,"E82"),sQuery(id+"F0.wireOp",EDGE,"E83")])]});
            var Q33;
            Q33=makeQuery(id+"F1.opExtrude","SWEPT_EDGE",EDGE,{"disambiguationData":[OSD([sQuery(id+"F0.wireOp",EDGE,"E71"),sQuery(id+"F0.wireOp",EDGE,"E72")])]});
            var Q34;
            Q34=makeQuery(id+"F1.opExtrude","SWEPT_EDGE",EDGE,{"disambiguationData":[OSD([sQuery(id+"F0.wireOp",EDGE,"E77"),sQuery(id+"F0.wireOp",EDGE,"E78")])]});
            var Q35;
            Q35=makeQuery(id+"F1.opExtrude","SWEPT_EDGE",EDGE,{"disambiguationData":[OSD([sQuery(id+"F0.wireOp",EDGE,"E76"),sQuery(id+"F0.wireOp",EDGE,"E77")])]});
            var Q36;
            Q36=makeQuery(id+"F1.opExtrude","SWEPT_EDGE",EDGE,{"disambiguationData":[OSD([sQuery(id+"F0.wireOp",EDGE,"E89"),sQuery(id+"F0.wireOp",EDGE,"E90")])]});
            var Q37;
            Q37=makeQuery(id+"F1.opExtrude","SWEPT_EDGE",EDGE,{"disambiguationData":[OSD([sQuery(id+"F0.wireOp",EDGE,"E90"),sQuery(id+"F0.wireOp",EDGE,"E91")])]});
            var Q38;
            Q38=makeQuery(id+"F1.opExtrude","SWEPT_EDGE",EDGE,{"disambiguationData":[OSD([sQuery(id+"F0.wireOp",EDGE,"E91"),sQuery(id+"F0.wireOp",EDGE,"E92")])]});
            var Q39;
            Q39=makeQuery(id+"F1.opExtrude","SWEPT_EDGE",EDGE,{"disambiguationData":[OSD([sQuery(id+"F0.wireOp",EDGE,"E88"),sQuery(id+"F0.wireOp",EDGE,"E89")])]});
            var Q40;
            Q40=makeQuery(id+"F1.opExtrude","SWEPT_EDGE",EDGE,{"disambiguationData":[OSD([sQuery(id+"F0.wireOp",EDGE,"E87"),sQuery(id+"F0.wireOp",EDGE,"E88")])]});
            var Q41;
            Q41=makeQuery(id+"F1.opExtrude","SWEPT_EDGE",EDGE,{"disambiguationData":[OSD([sQuery(id+"F0.wireOp",EDGE,"E86"),sQuery(id+"F0.wireOp",EDGE,"E87")])]});
            var Q42;
            Q42=makeQuery(id+"F1.opExtrude","SWEPT_EDGE",EDGE,{"disambiguationData":[OSD([sQuery(id+"F0.wireOp",EDGE,"E86"),sQuery(id+"F0.wireOp",EDGE,"E100")])]});
            var Q43;
            Q43=makeQuery(id+"F1.opExtrude","SWEPT_EDGE",EDGE,{"disambiguationData":[OSD([sQuery(id+"F0.wireOp",EDGE,"E98"),sQuery(id+"F0.wireOp",EDGE,"E99")])]});
            var Q44;
            Q44=makeQuery(id+"F1.opExtrude","SWEPT_EDGE",EDGE,{"disambiguationData":[OSD([sQuery(id+"F0.wireOp",EDGE,"E97"),sQuery(id+"F0.wireOp",EDGE,"E98")])]});
            var Q45;
            Q45=makeQuery(id+"F1.opExtrude","SWEPT_EDGE",EDGE,{"disambiguationData":[OSD([sQuery(id+"F0.wireOp",EDGE,"E96"),sQuery(id+"F0.wireOp",EDGE,"E97")])]});
            var Q46;
            Q46=makeQuery(id+"F1.opExtrude","SWEPT_EDGE",EDGE,{"disambiguationData":[OSD([sQuery(id+"F0.wireOp",EDGE,"E95"),sQuery(id+"F0.wireOp",EDGE,"E96")])]});
            var Q47;
            Q47=makeQuery(id+"F1.opExtrude","SWEPT_EDGE",EDGE,{"disambiguationData":[OSD([sQuery(id+"F0.wireOp",EDGE,"E94"),sQuery(id+"F0.wireOp",EDGE,"E95")])]});
            fillet(context, id + "F9", {"entities" : qUnion([Q0, Q1, Q2, Q3, Q4, Q5, Q6, Q7, Q8, Q9, Q10, Q11, Q12, Q13, Q14, Q15, Q16, Q17, Q18, Q19, Q20, Q21, Q22, Q23, Q24, Q25, Q26, Q27, Q28, Q29, Q30, Q31, Q32, Q33, Q34, Q35, Q36, Q37, Q38, Q39, Q40, Q41, Q42, Q43, Q44, Q45, Q46, Q47]), "radius" : .5 * mm, "tangentPropagation" : true, "allowEdgeOverflow" : false});
        }
        {
            var Q0;
            {var subQ0=sQuery(id+"F0.wireOp",EDGE,"E52");var subQ1=sQuery(id+"F0.wireOp",EDGE,"E51");var subQ2=sQuery(id+"F0.wireOp",EDGE,"E50");var subQ3=sQuery(id+"F0.wireOp",EDGE,"E42");var subQ4=sQuery(id+"F0.wireOp",EDGE,"E41");var subQ5=sQuery(id+"F0.wireOp",EDGE,"E49");var subQ6=sQuery(id+"F0.wireOp",EDGE,"E48");var subQ7=sQuery(id+"F0.wireOp",EDGE,"E47");var subQ8=sQuery(id+"F0.wireOp",EDGE,"E40");var subQ9=sQuery(id+"F0.wireOp",EDGE,"E105");var subQ10=sQuery(id+"F0.wireOp",EDGE,"E104");var subQ11=sQuery(id+"F0.wireOp",EDGE,"E46");var subQ12=sQuery(id+"F0.wireOp",EDGE,"E38");var subQ13=sQuery(id+"F0.wireOp",EDGE,"E103");var subQ14=sQuery(id+"F0.wireOp",EDGE,"E45");var subQ15=sQuery(id+"F0.wireOp",EDGE,"E44");var subQ16=sQuery(id+"F0.wireOp",EDGE,"E35");var subQ17=sQuery(id+"F0.wireOp",EDGE,"E69.filletArc");var subQ18=sQuery(id+"F0.wireOp",EDGE,"E68.filletArc");var subQ19=sQuery(id+"F0.wireOp",EDGE,"E67");var subQ20=sQuery(id+"F0.wireOp",EDGE,"E66");var subQ21=sQuery(id+"F0.wireOp",EDGE,"E65");var subQ22=sQuery(id+"F0.wireOp",EDGE,"E64");var subQ23=sQuery(id+"F0.wireOp",EDGE,"E63");var subQ24=sQuery(id+"F0.wireOp",EDGE,"E62");var subQ25=sQuery(id+"F0.wireOp",EDGE,"E61");var subQ26=sQuery(id+"F0.wireOp",EDGE,"E60");var subQ27=sQuery(id+"F0.wireOp",EDGE,"E59");var subQ28=sQuery(id+"F0.wireOp",EDGE,"E58");var subQ29=sQuery(id+"F0.wireOp",EDGE,"E57");var subQ30=sQuery(id+"F0.wireOp",EDGE,"E56");var subQ31=sQuery(id+"F0.wireOp",EDGE,"E55.filletArc");var subQ32=sQuery(id+"F0.wireOp",EDGE,"E54.filletArc");var subQ33=sQuery(id+"F0.wireOp",EDGE,"E53.filletArc");var subQ34=sQuery(id+"F0.wireOp",EDGE,"E43");var subQ35=sQuery(id+"F0.wireOp",EDGE,"E39");var subQ36=sQuery(id+"F0.wireOp",EDGE,"E37");var subQ37=sQuery(id+"F0.wireOp",EDGE,"E36");var subQ38=sQuery(id+"F0.wireOp",EDGE,"E34");var subQ39=sQuery(id+"F0.wireOp",EDGE,"E33");var subQ40=sQuery(id+"F0.wireOp",EDGE,"E32");var subQ41=sQuery(id+"F0.wireOp",EDGE,"E31");var subQ42=sQuery(id+"F0.wireOp",EDGE,"E110");var subQ43=sQuery(id+"F0.wireOp",EDGE,"E109");var subQ44=sQuery(id+"F0.wireOp",EDGE,"E108");var subQ45=sQuery(id+"F0.wireOp",EDGE,"E107");var subQ46=sQuery(id+"F0.wireOp",EDGE,"E106");var subQ47=sQuery(id+"F0.wireOp",EDGE,"E101.filletArc");var subQ48=sQuery(id+"F0.wireOp",EDGE,"E100");var subQ49=sQuery(id+"F0.wireOp",EDGE,"E99");var subQ50=sQuery(id+"F0.wireOp",EDGE,"E98");var subQ51=sQuery(id+"F0.wireOp",EDGE,"E97");var subQ52=sQuery(id+"F0.wireOp",EDGE,"E96");var subQ53=sQuery(id+"F0.wireOp",EDGE,"E95");var subQ54=sQuery(id+"F0.wireOp",EDGE,"E94");var subQ55=sQuery(id+"F0.wireOp",EDGE,"E93");var subQ56=sQuery(id+"F0.wireOp",EDGE,"E92");var subQ57=sQuery(id+"F0.wireOp",EDGE,"E91");var subQ58=sQuery(id+"F0.wireOp",EDGE,"E90");var subQ59=sQuery(id+"F0.wireOp",EDGE,"E89");var subQ60=sQuery(id+"F0.wireOp",EDGE,"E88");var subQ61=sQuery(id+"F0.wireOp",EDGE,"E87");var subQ62=sQuery(id+"F0.wireOp",EDGE,"E86");var subQ63=sQuery(id+"F0.wireOp",EDGE,"E84");var subQ64=sQuery(id+"F0.wireOp",EDGE,"E83");var subQ65=sQuery(id+"F0.wireOp",EDGE,"E82");var subQ66=sQuery(id+"F0.wireOp",EDGE,"E81");var subQ67=sQuery(id+"F0.wireOp",EDGE,"E80");var subQ68=sQuery(id+"F0.wireOp",EDGE,"E79");var subQ69=sQuery(id+"F0.wireOp",EDGE,"E78");var subQ70=sQuery(id+"F0.wireOp",EDGE,"E77");var subQ71=sQuery(id+"F0.wireOp",EDGE,"E76");var subQ72=sQuery(id+"F0.wireOp",EDGE,"E75");var subQ73=sQuery(id+"F0.wireOp",EDGE,"E74");var subQ74=sQuery(id+"F0.wireOp",EDGE,"E73");var subQ75=sQuery(id+"F0.wireOp",EDGE,"E72");var subQ76=sQuery(id+"F0.wireOp",EDGE,"E71");var subQ77=sQuery(id+"F0.wireOp",EDGE,"E70");var subQ78=sQuery(id+"F0.wireOp",EDGE,"E29.filletArc");var subQ79=sQuery(id+"F0.wireOp",EDGE,"E28.filletArc");var subQ80=sQuery(id+"F0.wireOp",EDGE,"E27");var subQ81=sQuery(id+"F0.wireOp",EDGE,"E26");var subQ82=sQuery(id+"F0.wireOp",EDGE,"E25");var subQ83=sQuery(id+"F0.wireOp",EDGE,"E24");var subQ84=sQuery(id+"F0.wireOp",EDGE,"E22");var subQ85=sQuery(id+"F0.wireOp",EDGE,"E21");var subQ86=sQuery(id+"F0.wireOp",EDGE,"E19");var subQ87=sQuery(id+"F0.wireOp",EDGE,"E18");var subQ88=sQuery(id+"F0.wireOp",EDGE,"E17");var subQ89=sQuery(id+"F0.wireOp",EDGE,"E16");var subQ90=sQuery(id+"F0.wireOp",EDGE,"E15");var subQ91=sQuery(id+"F0.wireOp",EDGE,"E14");var subQ92=sQuery(id+"F0.wireOp",EDGE,"E13");var subQ93=sQuery(id+"F0.wireOp",EDGE,"E12");var subQ94=sQuery(id+"F0.wireOp",EDGE,"E11");var subQ95=sQuery(id+"F0.wireOp",EDGE,"E10");var subQ96=sQuery(id+"F0.wireOp",EDGE,"E9");var subQ97=sQuery(id+"F0.wireOp",EDGE,"E8");var subQ98=sQuery(id+"F0.wireOp",EDGE,"E7");var subQ99=sQuery(id+"F0.wireOp",EDGE,"E6");var subQ100=sQuery(id+"F0.wireOp",EDGE,"E5");var subQ101=sQuery(id+"F0.wireOp",EDGE,"E4");Q0=makeQuery(id+"F6.opBoolean","MERGE",FACE,{"derivedFrom":[makeQuery(id+"F1.opExtrude","CAP_FACE",FACE,{"disambiguationData":[OSD([subQ101,subQ100,subQ99,subQ98,subQ97,subQ96,subQ95,subQ94,subQ93,subQ92])],"isStart":true}),makeQuery(id+"F1.opExtrude","CAP_FACE",FACE,{"disambiguationData":[OSD([subQ91,subQ90,subQ89,subQ88,subQ87,subQ86,subQ85,subQ84,subQ79,subQ78,subQ46,subQ45,subQ44,subQ43,subQ42])],"isStart":true}),makeQuery(id+"F1.opExtrude","CAP_FACE",FACE,{"disambiguationData":[OSD([subQ83,subQ82,subQ81,subQ80])],"isStart":true}),makeQuery(id+"F1.opExtrude","CAP_FACE",FACE,{"disambiguationData":[OSD([subQ77,subQ76,subQ75,subQ74,subQ73,subQ72,subQ71,subQ70,subQ69,subQ68,subQ67,subQ66,subQ65,subQ64,subQ63])],"isStart":true}),makeQuery(id+"F1.opExtrude","CAP_FACE",FACE,{"disambiguationData":[OSD([subQ62,subQ61,subQ60,subQ59,subQ58,subQ57,subQ56,subQ55,subQ54,subQ53,subQ52,subQ51,subQ50,subQ49,subQ48,subQ47])],"isStart":true}),makeQuery(id+"F4.opExtrude","CAP_FACE",FACE,{"disambiguationData":[OSD([subQ101,subQ100,subQ99,subQ98,subQ97,subQ96,subQ95,subQ94,subQ93,subQ92,subQ91,subQ90,subQ89,subQ88,subQ87,subQ86,subQ85,subQ84,subQ83,subQ82,subQ81,subQ80,subQ79,subQ78,subQ41,subQ40,subQ39,subQ38,subQ16,subQ37,subQ36,subQ12,subQ35,subQ8,subQ3,subQ34,subQ15,subQ14,subQ11,subQ7,subQ6,subQ5,subQ2,subQ1,subQ0,subQ33,subQ32,subQ31,subQ30,subQ29,subQ28,subQ27,subQ26,subQ25,subQ24,subQ23,subQ22,subQ21,subQ20,subQ19,subQ18,subQ17,subQ77,subQ76,subQ75,subQ74,subQ73,subQ72,subQ71,subQ70,subQ69,subQ68,subQ67,subQ66,subQ65,subQ64,subQ63,subQ62,subQ61,subQ60,subQ59,subQ58,subQ57,subQ56,subQ55,subQ54,subQ53,subQ52,subQ51,subQ50,subQ49,subQ48,subQ47,sQuery(id+"F0.wireOp",EDGE,"E102.0"),sQuery(id+"F0.wireOp",EDGE,"E102.1"),sQuery(id+"F0.wireOp",EDGE,"E102.2"),sQuery(id+"F0.wireOp",EDGE,"E102.3")])],"isStart":true}),makeQuery(id+"F4.opExtrude","CAP_FACE",FACE,{"disambiguationData":[OSD([subQ46,subQ45,subQ44,subQ43,subQ42])],"isStart":true}),makeQuery(id+"F2.boolean.opBoolean","MERGE",FACE,{"derivedFrom":[makeQuery(id+"F1.opExtrude","CAP_FACE",FACE,{"disambiguationData":[OSD([subQ41,subQ40,subQ39,subQ38,subQ37,subQ36,subQ35,subQ8,subQ4,subQ3,subQ34,subQ33,subQ32,subQ31,subQ30,subQ29,subQ28,subQ27,subQ26,subQ25,subQ24,subQ23,subQ22,subQ21,subQ20,subQ19,subQ18,subQ17,subQ13,subQ10,subQ9])],"isStart":true}),makeQuery(id+"F2.opExtrude","CAP_FACE",FACE,{"disambiguationData":[OSD([subQ16,subQ15,subQ14,subQ13])],"isStart":true}),makeQuery(id+"F2.opExtrude","CAP_FACE",FACE,{"disambiguationData":[OSD([subQ12,subQ11,subQ10,subQ9])],"isStart":true}),makeQuery(id+"F2.opExtrude","CAP_FACE",FACE,{"disambiguationData":[OSD([subQ8,subQ7,subQ6,subQ5])],"isStart":true}),makeQuery(id+"F2.opExtrude","CAP_FACE",FACE,{"disambiguationData":[OSD([subQ4,subQ3,subQ2,subQ1,subQ0])],"isStart":true})]})]});}
            fillet(context, id + "F10", {"entities" : qUnion([Q0]), "radius" : .5 * mm, "tangentPropagation" : true, "allowEdgeOverflow" : false});
        }
        {
            var Q0;
            Q0=makeQuery(id+"F1.opExtrude","CAP_FACE",FACE,{"disambiguationData":[OSD([sQuery(id+"F0.wireOp",EDGE,"E4"),sQuery(id+"F0.wireOp",EDGE,"E5"),sQuery(id+"F0.wireOp",EDGE,"E6"),sQuery(id+"F0.wireOp",EDGE,"E7"),sQuery(id+"F0.wireOp",EDGE,"E8"),sQuery(id+"F0.wireOp",EDGE,"E9"),sQuery(id+"F0.wireOp",EDGE,"E10"),sQuery(id+"F0.wireOp",EDGE,"E11"),sQuery(id+"F0.wireOp",EDGE,"E12"),sQuery(id+"F0.wireOp",EDGE,"E13")])],"isStart":false});
            var Q1;
            Q1=makeQuery(id+"F1.opExtrude","CAP_FACE",FACE,{"disambiguationData":[OSD([sQuery(id+"F0.wireOp",EDGE,"E14"),sQuery(id+"F0.wireOp",EDGE,"E15"),sQuery(id+"F0.wireOp",EDGE,"E16"),sQuery(id+"F0.wireOp",EDGE,"E17"),sQuery(id+"F0.wireOp",EDGE,"E18"),sQuery(id+"F0.wireOp",EDGE,"E19"),sQuery(id+"F0.wireOp",EDGE,"E21"),sQuery(id+"F0.wireOp",EDGE,"E22"),sQuery(id+"F0.wireOp",EDGE,"E28.filletArc"),sQuery(id+"F0.wireOp",EDGE,"E29.filletArc"),sQuery(id+"F0.wireOp",EDGE,"E106"),sQuery(id+"F0.wireOp",EDGE,"E107"),sQuery(id+"F0.wireOp",EDGE,"E108"),sQuery(id+"F0.wireOp",EDGE,"E109"),sQuery(id+"F0.wireOp",EDGE,"E110")])],"isStart":false});
            var Q2;
            Q2=makeQuery(id+"F1.opExtrude","CAP_FACE",FACE,{"disambiguationData":[OSD([sQuery(id+"F0.wireOp",EDGE,"E24"),sQuery(id+"F0.wireOp",EDGE,"E25"),sQuery(id+"F0.wireOp",EDGE,"E26"),sQuery(id+"F0.wireOp",EDGE,"E27")])],"isStart":false});
            var Q3;
            Q3=makeQuery(id+"F1.opExtrude","CAP_FACE",FACE,{"disambiguationData":[OSD([sQuery(id+"F0.wireOp",EDGE,"E70"),sQuery(id+"F0.wireOp",EDGE,"E71"),sQuery(id+"F0.wireOp",EDGE,"E72"),sQuery(id+"F0.wireOp",EDGE,"E73"),sQuery(id+"F0.wireOp",EDGE,"E74"),sQuery(id+"F0.wireOp",EDGE,"E75"),sQuery(id+"F0.wireOp",EDGE,"E76"),sQuery(id+"F0.wireOp",EDGE,"E77"),sQuery(id+"F0.wireOp",EDGE,"E78"),sQuery(id+"F0.wireOp",EDGE,"E79"),sQuery(id+"F0.wireOp",EDGE,"E80"),sQuery(id+"F0.wireOp",EDGE,"E81"),sQuery(id+"F0.wireOp",EDGE,"E82"),sQuery(id+"F0.wireOp",EDGE,"E83"),sQuery(id+"F0.wireOp",EDGE,"E84")])],"isStart":false});
            fillet(context, id + "F11", {"entities" : qUnion([Q0, Q1, Q2, Q3]), "radius" : .3 * mm, "tangentPropagation" : true, "allowEdgeOverflow" : false});
        }
        {
            var Q0;
            Q0=makeQuery(id+"F1.opExtrude","CAP_EDGE",EDGE,{"disambiguationData":[OSD([sQuery(id+"F0.wireOp",EDGE,"E34")])],"isStart":false});
            var Q1;
            Q1=makeQuery(id+"F1.opExtrude","CAP_EDGE",EDGE,{"disambiguationData":[OSD([sQuery(id+"F0.wireOp",EDGE,"E57")])],"isStart":false});
            var Q2;
            Q2=makeQuery(id+"F1.opExtrude","CAP_EDGE",EDGE,{"disambiguationData":[OSD([sQuery(id+"F0.wireOp",EDGE,"E56")])],"isStart":false});
            fillet(context, id + "F12", {"entities" : qUnion([Q0, Q1, Q2]), "radius" : .5 * mm, "tangentPropagation" : true, "allowEdgeOverflow" : false});
        }
        {
            var Q0;
            Q0=makeQuery(id+"F1.opExtrude","CAP_FACE",FACE,{"disambiguationData":[OSD([sQuery(id+"F0.wireOp",EDGE,"E86"),sQuery(id+"F0.wireOp",EDGE,"E87"),sQuery(id+"F0.wireOp",EDGE,"E88"),sQuery(id+"F0.wireOp",EDGE,"E89"),sQuery(id+"F0.wireOp",EDGE,"E90"),sQuery(id+"F0.wireOp",EDGE,"E91"),sQuery(id+"F0.wireOp",EDGE,"E92"),sQuery(id+"F0.wireOp",EDGE,"E93"),sQuery(id+"F0.wireOp",EDGE,"E94"),sQuery(id+"F0.wireOp",EDGE,"E95"),sQuery(id+"F0.wireOp",EDGE,"E96"),sQuery(id+"F0.wireOp",EDGE,"E97"),sQuery(id+"F0.wireOp",EDGE,"E98"),sQuery(id+"F0.wireOp",EDGE,"E99"),sQuery(id+"F0.wireOp",EDGE,"E100"),sQuery(id+"F0.wireOp",EDGE,"E101.filletArc")])],"isStart":false});
            fillet(context, id + "F13", {"entities" : qUnion([Q0]), "radius" : .5 * mm, "tangentPropagation" : true, "allowEdgeOverflow" : false});
        }
        {
            var Q0;
            Q0=qCreatedBy(makeId("Front.planeOp"),FACE);
            var sketch = newSketch(context, id + "F14", { "sketchPlane" : qUnion([Q0])});
            skCircle(sketch, "E111", {"center": v(-30.54, 6.15) * mm, "radius": 1.25 * mm});
            skCircle(sketch, "E112", {"center": v(-30.54, 6.15) * mm, "radius": 3.25 * mm});
            skSolve(sketch);
        }
        {
            var Q0;
            Q0=makeQuery(id+"F14.imprint","IMPRINT",FACE,{"disambiguationData":[TD([[makeQuery(id+"F14.imprint","IMPRINT",EDGE,{"derivedFrom":sQuery(id+"F14.wireOp",EDGE,"E111")}),-1.0]])]});
            var Q1;
            Q1=makeQuery(id+"F3.opExtrude","CAP_FACE",FACE,{"disambiguationData":[OSD([sQuery(id+"F0.wireOp",EDGE,"E0"),sQuery(id+"F0.wireOp",EDGE,"E1"),sQuery(id+"F0.wireOp",EDGE,"E2"),sQuery(id+"F0.wireOp",EDGE,"E3"),sQuery(id+"F0.wireOp",EDGE,"E102.0"),sQuery(id+"F0.wireOp",EDGE,"E102.1"),sQuery(id+"F0.wireOp",EDGE,"E102.2"),sQuery(id+"F0.wireOp",EDGE,"E102.3")])],"isStart":false});
            var Q2;
            Q2=makeQuery(id+"F3.opExtrude","CAP_FACE",FACE,{"disambiguationData":[OSD([sQuery(id+"F0.wireOp",EDGE,"E0"),sQuery(id+"F0.wireOp",EDGE,"E1"),sQuery(id+"F0.wireOp",EDGE,"E2"),sQuery(id+"F0.wireOp",EDGE,"E3"),sQuery(id+"F0.wireOp",EDGE,"E102.0"),sQuery(id+"F0.wireOp",EDGE,"E102.1"),sQuery(id+"F0.wireOp",EDGE,"E102.2"),sQuery(id+"F0.wireOp",EDGE,"E102.3")])],"isStart":true});
            extrude(context, id + "F15", {"entities" : qUnion([Q0]), "operationType" : NewBodyOperationType.ADD, "endBound" : BoundingType.UP_TO_SURFACE, "endBoundEntityFace" : qUnion([Q1]), "depth" : 25 * mm, "hasSecondDirection" : true, "secondDirectionBound" : SecondDirectionBoundingType.UP_TO_SURFACE, "secondDirectionOppositeDirection" : true, "secondDirectionBoundEntityFace" : qUnion([Q2]), "secondDirectionDepth" : 25 * mm});
        }
        {
            var Q0;
            Q0=makeQuery(id+"F15.boolean.opBoolean","INTERSECT",EDGE,{"derivedFrom":[makeQuery(id+"F3.opExtrude","SWEPT_FACE",FACE,{"disambiguationData":[OSD([sQuery(id+"F0.wireOp",EDGE,"E2")])]}),makeQuery(id+"F15.opExtrude","SWEPT_FACE",FACE,{"disambiguationData":[OSD([sQuery(id+"F14.wireOp",EDGE,"E112")])]})]});
            var Q1;
            Q1=makeQuery(id+"F15.boolean.opBoolean","INTERSECT",EDGE,{"derivedFrom":[makeQuery(id+"F3.opExtrude","SWEPT_FACE",FACE,{"disambiguationData":[OSD([sQuery(id+"F0.wireOp",EDGE,"E3")])]}),makeQuery(id+"F15.opExtrude","SWEPT_FACE",FACE,{"disambiguationData":[OSD([sQuery(id+"F14.wireOp",EDGE,"E112")])]})]});
            fillet(context, id + "F16", {"entities" : qUnion([Q0, Q1]), "radius" : 5 * mm, "tangentPropagation" : true, "allowEdgeOverflow" : false});
        }
        {
            var Q0;
            Q0=makeQuery(id+"F3.opExtrude","CAP_EDGE",EDGE,{"disambiguationData":[OSD([sQuery(id+"F0.wireOp",EDGE,"E2")])],"isStart":false});
            var Q1;
            Q1=makeQuery(id+"F15.opExtrude","CAP_EDGE",EDGE,{"disambiguationData":[OSD([sQuery(id+"F14.wireOp",EDGE,"E112")])],"isStart":false});
            var Q2;
            {var subQ0=sQuery(id+"F14.wireOp",EDGE,"E112");var subQ2=sQuery(id+"F0.wireOp",EDGE,"E2");Q2=makeQuery(id+"F15.boolean.opBoolean","SPLIT",EDGE,{"disambiguationData":[TD([makeQuery(id+"F3.opExtrude","SWEPT_FACE",FACE,{"disambiguationData":[OSD([subQ2])]})])],"derivedFrom":makeQuery(id+"F15.opExtrude","CAP_EDGE",EDGE,{"disambiguationData":[OSD([subQ0])],"isStart":true})});}
            var Q3;
            Q3=makeQuery(id+"F3.opExtrude","CAP_EDGE",EDGE,{"disambiguationData":[OSD([sQuery(id+"F0.wireOp",EDGE,"E3")])],"isStart":true});
            var Q4;
            Q4=makeQuery(id+"F15.opExtrude","CAP_EDGE",EDGE,{"disambiguationData":[OSD([sQuery(id+"F14.wireOp",EDGE,"E111")])],"isStart":false});
            var Q5;
            Q5=makeQuery(id+"F15.opExtrude","CAP_EDGE",EDGE,{"disambiguationData":[OSD([sQuery(id+"F14.wireOp",EDGE,"E111")])],"isStart":true});
            fillet(context, id + "F17", {"entities" : qUnion([Q0, Q1, Q2, Q3, Q4, Q5]), "radius" : .5 * mm, "tangentPropagation" : true, "allowEdgeOverflow" : false});
        }
    });
